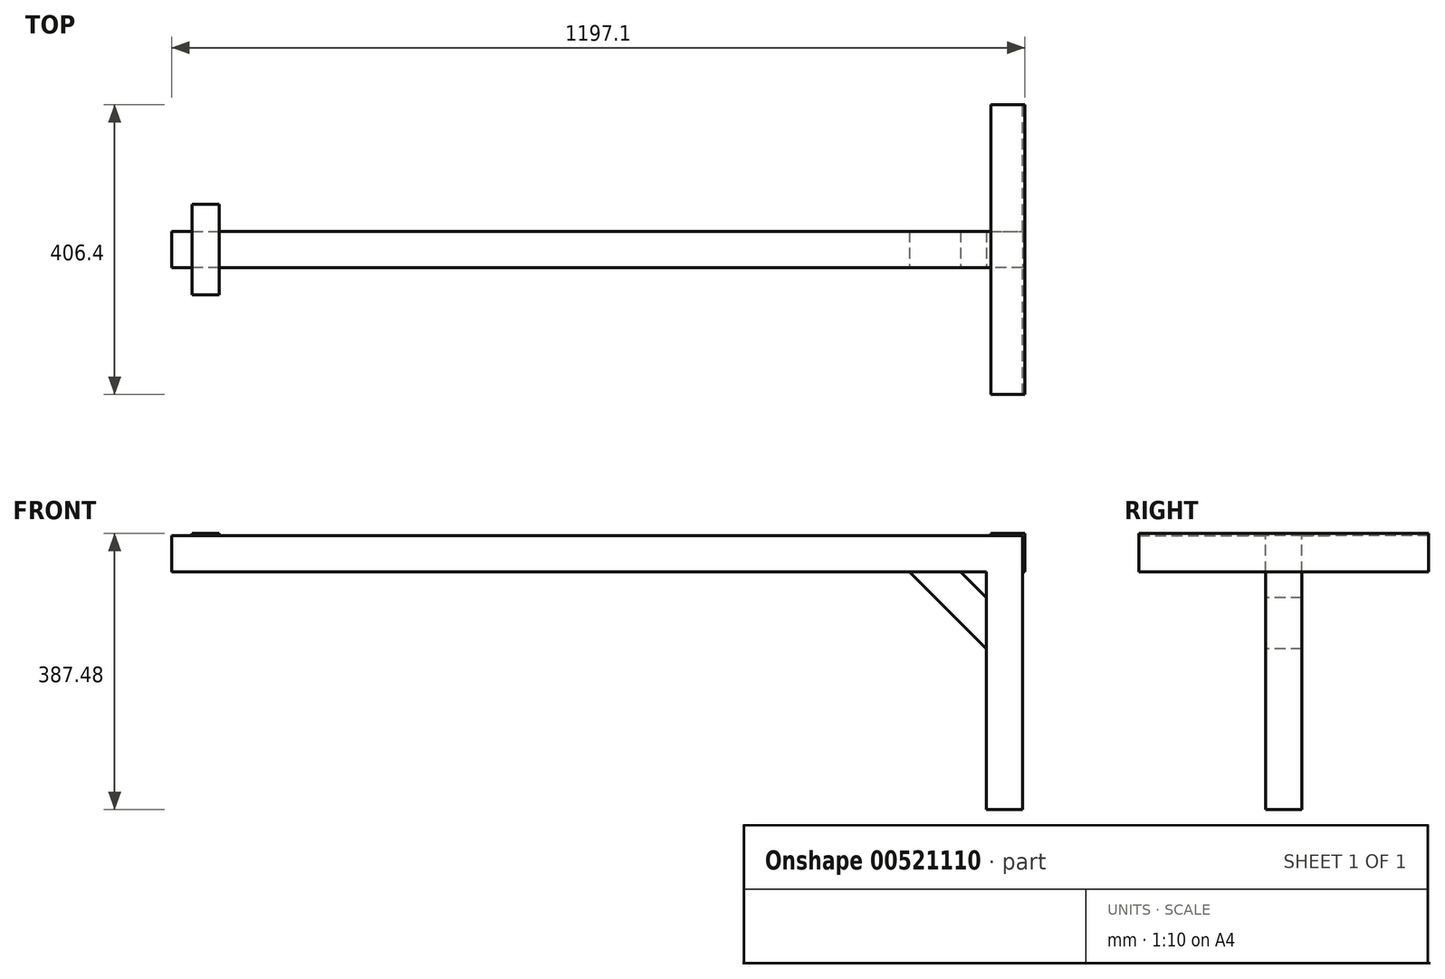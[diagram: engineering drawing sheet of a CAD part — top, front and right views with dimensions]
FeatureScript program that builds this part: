
annotation { "Feature Type Name" : "Feature", "Feature Type Description" : "" }
export const myFeature = defineFeature(function(context is Context, id is Id, definition is map)
    precondition{}
    {
        {
            var Q0;
            Q0=qCreatedBy(makeId("Top.planeOp"),FACE);
            var sketch = newSketch(context, id + "F0", { "sketchPlane" : qUnion([Q0])});
            skLineSegment(sketch, "E0.bottom", {"start": v(25.4, 203.2) * mm, "end": v(-25.4, 203.2) * mm});
            skLineSegment(sketch, "E0.top", {"start": v(25.4, -203.2) * mm, "end": v(-25.4, -203.2) * mm});
            skLineSegment(sketch, "E0.left", {"start": v(25.4, 203.2) * mm, "end": v(25.4, -203.2) * mm});
            skLineSegment(sketch, "E0.right", {"start": v(-25.4, 203.2) * mm, "end": v(-25.4, -203.2) * mm});
            skPoint(sketch, "E0.middle", {"position": v(0, 0) * mm});
            skSolve(sketch);
        }
        {
            var Q0;
            Q0=makeQuery(id+"F0.imprint","IMPRINT",FACE,{"disambiguationData":[TD([[makeQuery(id+"F0.imprint","IMPRINT",EDGE,{"derivedFrom":sQuery(id+"F0.wireOp",EDGE,"E0.bottom")}),1.0]])]});
            extrude(context, id + "F1", {"entities" : qUnion([Q0]), "depth" : 6.35 * mm, "offsetDistance" : 25.4 * mm});
        }
        {
            var Q0;
            Q0=makeQuery(id+"F1.opExtrude","CAP_FACE",FACE,{"disambiguationData":[OSD([sQuery(id+"F0.wireOp",EDGE,"E0.bottom"),sQuery(id+"F0.wireOp",EDGE,"E0.top"),sQuery(id+"F0.wireOp",EDGE,"E0.left"),sQuery(id+"F0.wireOp",EDGE,"E0.right")])],"isStart":true});
            var sketch = newSketch(context, id + "F2", { "sketchPlane" : qUnion([Q0])});
            skLineSegment(sketch, "E1.bottom", {"start": v(25.4, 203.2) * mm, "end": v(19.05, 203.2) * mm});
            skLineSegment(sketch, "E1.top", {"start": v(25.4, -203.2) * mm, "end": v(19.05, -203.2) * mm});
            skLineSegment(sketch, "E1.left", {"start": v(25.4, 203.2) * mm, "end": v(25.4, -203.2) * mm});
            skLineSegment(sketch, "E1.right", {"start": v(19.05, 203.2) * mm, "end": v(19.05, -203.2) * mm});
            skSolve(sketch);
        }
        {
            var Q0;
            Q0=makeQuery(id+"F2.imprint","IMPRINT",FACE,{"disambiguationData":[TD([[makeQuery(id+"F2.imprint","IMPRINT",EDGE,{"derivedFrom":sQuery(id+"F2.wireOp",EDGE,"E1.bottom")}),1.0]])]});
            extrude(context, id + "F3", {"entities" : qUnion([Q0]), "operationType" : NewBodyOperationType.ADD, "depth" : 50.8 * mm, "offsetDistance" : 25.4 * mm});
        }
        {
            var Q0;
            Q0=makeQuery(id+"F3.boolean.opBoolean","MERGE",FACE,{"derivedFrom":[makeQuery(id+"F1.opExtrude","SWEPT_FACE",FACE,{"disambiguationData":[OSD([sQuery(id+"F0.wireOp",EDGE,"E0.left")])]}),makeQuery(id+"F3.opExtrude","SWEPT_FACE",FACE,{"disambiguationData":[OSD([sQuery(id+"F2.wireOp",EDGE,"E1.left")])]})]});
            extrude(context, id + "F4", {"entities" : qUnion([Q0]), "operationType" : NewBodyOperationType.REMOVE, "oppositeDirection" : true, "depth" : 3.05 * mm, "offsetDistance" : 25.4 * mm});
        }
        {
            var Q0;
            Q0=makeQuery(id+"F1.opExtrude","CAP_FACE",FACE,{"disambiguationData":[OSD([sQuery(id+"F0.wireOp",EDGE,"E0.bottom"),sQuery(id+"F0.wireOp",EDGE,"E0.top"),sQuery(id+"F0.wireOp",EDGE,"E0.left"),sQuery(id+"F0.wireOp",EDGE,"E0.right")])],"isStart":false});
            extrude(context, id + "F5", {"entities" : qUnion([Q0]), "operationType" : NewBodyOperationType.REMOVE, "oppositeDirection" : true, "depth" : 3.05 * mm, "offsetDistance" : 25.4 * mm});
        }
        {
            var Q0;
            Q0=makeQuery(id+"F1.opExtrude","CAP_FACE",FACE,{"disambiguationData":[OSD([sQuery(id+"F0.wireOp",EDGE,"E0.bottom"),sQuery(id+"F0.wireOp",EDGE,"E0.top"),sQuery(id+"F0.wireOp",EDGE,"E0.left"),sQuery(id+"F0.wireOp",EDGE,"E0.right")])],"isStart":true});
            var sketch = newSketch(context, id + "F6", { "sketchPlane" : qUnion([Q0])});
            skLineSegment(sketch, "E2", {"start": v(19.05, 0) * mm, "end": v(19.05, 25.4) * mm});
            skLineSegment(sketch, "E3", {"start": v(19.05, 25.4) * mm, "end": v(-1174.75, 25.4) * mm});
            skLineSegment(sketch, "E4", {"start": v(-1174.75, 25.4) * mm, "end": v(-1174.75, -25.4) * mm});
            skLineSegment(sketch, "E5", {"start": v(-1174.75, -25.4) * mm, "end": v(19.05, -25.4) * mm});
            skLineSegment(sketch, "E6", {"start": v(19.05, -25.4) * mm, "end": v(19.05, 25.4) * mm});
            skSolve(sketch);
        }
        {
            var Q0;
            {var subQ1=sQuery(id+"F6.wireOp",EDGE,"E3");var subQ4=makeQuery(id+"F1.opExtrude","CAP_EDGE",EDGE,{"disambiguationData":[OSD([sQuery(id+"F0.wireOp",EDGE,"E0.right")])],"isStart":true});var subQ5=makeQuery(id+"F6.imprint","INTERSECT",VERTEX,{"derivedFrom":[subQ4,subQ1]});Q0=makeQuery(id+"F6.imprint","IMPRINT",FACE,{"disambiguationData":[TD([[makeQuery(id+"F6.imprint","IMPRINT",EDGE,{"disambiguationData":[TD([[subQ5,1.0]])],"derivedFrom":subQ4}),-1.0]])]});}
            var Q1;
            {var subQ0=sQuery(id+"F6.wireOp",EDGE,"E4");Q1=makeQuery(id+"F6.imprint","IMPRINT",FACE,{"disambiguationData":[TD([[makeQuery(id+"F6.imprint","IMPRINT",EDGE,{"derivedFrom":subQ0}),1.0]])]});}
            extrude(context, id + "F7", {"entities" : qUnion([Q0, Q1]), "operationType" : NewBodyOperationType.ADD, "depth" : 50.8 * mm, "offsetDistance" : 25.4 * mm});
        }
        {
            var Q0;
            Q0=makeQuery(id+"F7.opExtrude","CAP_FACE",FACE,{"disambiguationData":[OSD([sQuery(id+"F6.wireOp",EDGE,"E3"),sQuery(id+"F6.wireOp",EDGE,"E4"),sQuery(id+"F6.wireOp",EDGE,"E5"),sQuery(id+"F6.wireOp",EDGE,"E6")])],"isStart":true});
            var sketch = newSketch(context, id + "F8", { "sketchPlane" : qUnion([Q0])});
            skLineSegment(sketch, "E7", {"start": v(-1174.75, 25.4) * mm, "end": v(-1146.05, 25.4) * mm});
            skLineSegment(sketch, "E8", {"start": v(-1146.05, 25.4) * mm, "end": v(-1146.05, 63.5) * mm});
            skLineSegment(sketch, "E9", {"start": v(-1146.05, 63.5) * mm, "end": v(-1107.95, 63.5) * mm});
            skLineSegment(sketch, "E10", {"start": v(-1107.95, 63.5) * mm, "end": v(-1107.95, -25.4) * mm});
            skLineSegment(sketch, "E11", {"start": v(-1107.95, -25.4) * mm, "end": v(-1107.95, -63.5) * mm});
            skLineSegment(sketch, "E12", {"start": v(-1107.95, -63.5) * mm, "end": v(-1146.05, -63.5) * mm});
            skLineSegment(sketch, "E13", {"start": v(-1146.05, -63.5) * mm, "end": v(-1146.05, 25.4) * mm});
            skSolve(sketch);
        }
        {
            var Q0;
            {var subQ0=sQuery(id+"F8.wireOp",EDGE,"E11");Q0=makeQuery(id+"F8.imprint","IMPRINT",FACE,{"disambiguationData":[TD([[makeQuery(id+"F8.imprint","IMPRINT",EDGE,{"derivedFrom":subQ0}),-1.0]])]});}
            var Q1;
            {var subQ0=sQuery(id+"F8.wireOp",EDGE,"E10");var subQ1=sQuery(id+"F6.wireOp",EDGE,"E3");var subQ2=sQuery(id+"F6.wireOp",EDGE,"E5");var subQ3=makeQuery(id+"F7.opExtrude","CAP_FACE",FACE,{"disambiguationData":[OSD([subQ1,sQuery(id+"F6.wireOp",EDGE,"E4"),subQ2,sQuery(id+"F6.wireOp",EDGE,"E6")])],"isStart":true});var subQ6=makeQuery(id+"F7.boolean.opBoolean","SPLIT",EDGE,{"disambiguationData":[topologyDisambiguationEdgeConnected([subQ3])],"derivedFrom":makeQuery(id+"F7.opExtrude","CAP_EDGE",EDGE,{"disambiguationData":[OSD([subQ2])],"isStart":true})});var subQ7=makeQuery(id+"F8.imprint","INTERSECT",VERTEX,{"derivedFrom":[subQ6,subQ0]});Q1=makeQuery(id+"F8.imprint","IMPRINT",FACE,{"disambiguationData":[TD([[makeQuery(id+"F8.imprint","IMPRINT",EDGE,{"disambiguationData":[TD([[subQ7,-1.0]])],"derivedFrom":subQ0}),-1.0]])]});}
            var Q2;
            {var subQ0=sQuery(id+"F8.wireOp",EDGE,"E8");Q2=makeQuery(id+"F8.imprint","IMPRINT",FACE,{"disambiguationData":[TD([[makeQuery(id+"F8.imprint","IMPRINT",EDGE,{"derivedFrom":subQ0}),-1.0]])]});}
            extrude(context, id + "F9", {"entities" : qUnion([Q0, Q1, Q2]), "operationType" : NewBodyOperationType.ADD, "depth" : 3.05 * mm, "offsetDistance" : 25.4 * mm});
        }
        {
            var Q0;
            Q0=makeQuery(id+"F7.boolean.opBoolean","MERGE",FACE,{"derivedFrom":[makeQuery(id+"F3.opExtrude","CAP_FACE",FACE,{"disambiguationData":[OSD([sQuery(id+"F2.wireOp",EDGE,"E1.bottom"),sQuery(id+"F2.wireOp",EDGE,"E1.top"),sQuery(id+"F2.wireOp",EDGE,"E1.left"),sQuery(id+"F2.wireOp",EDGE,"E1.right")])],"isStart":false}),makeQuery(id+"F7.opExtrude","CAP_FACE",FACE,{"disambiguationData":[OSD([sQuery(id+"F6.wireOp",EDGE,"E3"),sQuery(id+"F6.wireOp",EDGE,"E4"),sQuery(id+"F6.wireOp",EDGE,"E5"),sQuery(id+"F6.wireOp",EDGE,"E6")])],"isStart":false})]});
            var sketch = newSketch(context, id + "F10", { "sketchPlane" : qUnion([Q0])});
            skLineSegment(sketch, "E14", {"start": v(19.05, -25.4) * mm, "end": v(19.05, 25.4) * mm});
            skLineSegment(sketch, "E15", {"start": v(19.05, 25.4) * mm, "end": v(-31.75, 25.4) * mm});
            skLineSegment(sketch, "E16", {"start": v(-31.75, 25.4) * mm, "end": v(-31.75, -25.4) * mm});
            skLineSegment(sketch, "E17", {"start": v(-31.75, -25.4) * mm, "end": v(19.05, -25.4) * mm});
            skSolve(sketch);
        }
        {
            var Q0;
            Q0 = qSketchRegion(id + "F10", true);
            extrude(context, id + "F11", {"entities" : qUnion([Q0]), "operationType" : NewBodyOperationType.ADD, "depth" : 333.38 * mm, "offsetDistance" : 25.4 * mm});
        }
        {
            var Q0;
            Q0=makeQuery(id+"F11.boolean.opBoolean","MERGE",FACE,{"derivedFrom":[makeQuery(id+"F7.opExtrude","SWEPT_FACE",FACE,{"disambiguationData":[OSD([sQuery(id+"F6.wireOp",EDGE,"E3")])]}),makeQuery(id+"F11.opExtrude","SWEPT_FACE",FACE,{"disambiguationData":[OSD([sQuery(id+"F10.wireOp",EDGE,"E15")])]})]});
            var sketch = newSketch(context, id + "F12", { "sketchPlane" : qUnion([Q0])});
            skLineSegment(sketch, "E18", {"start": v(-31.75, -50.8) * mm, "end": v(-139.7, -50.8) * mm});
            skLineSegment(sketch, "E19", {"start": v(-31.75, -158.75) * mm, "end": v(-139.7, -50.8) * mm});
            skLineSegment(sketch, "E20", {"start": v(-49.8, -68.85) * mm, "end": v(-67.76, -50.9) * mm});
            skPoint(sketch, "E20.endSnap0", {"position": v(-67.76, -86.81) * mm});
            skLineSegment(sketch, "E21", {"start": v(-67.76, -50.9) * mm, "end": v(-31.75, -86.9) * mm});
            skLineSegment(sketch, "E22", {"start": v(-139.7, -50.8) * mm, "end": v(-67.76, -50.9) * mm});
            skLineSegment(sketch, "E23", {"start": v(-31.75, -86.9) * mm, "end": v(-31.75, -158.75) * mm});
            skSolve(sketch);
        }
        {
            var Q0;
            Q0=makeQuery(id+"F12.imprint","IMPRINT",FACE,{"disambiguationData":[TD([[makeQuery(id+"F12.imprint","IMPRINT",EDGE,{"derivedFrom":sQuery(id+"F12.wireOp",EDGE,"E19")}),-1.0]])]});
            extrude(context, id + "F13", {"entities" : qUnion([Q0]), "oppositeDirection" : true, "depth" : 50.8 * mm, "offsetDistance" : 25.4 * mm});
        }
    });
